# Revit family: PRD_FrankeWS_UrnlFlshngVlvs_BasicInstallationKitsForFlushingSystems_AQLN0006
name_source: partatom
category: Plumbing Fixtures
revit_build: Autodesk Revit 2018 (Build: 20190510_1515(x64)
units: mm (PartAtom-declared; Revit-internal decimal feet)

## family parameters
Cut with Voids When Loaded = No
Host = Face
OmniClass Number = 23.45.05.14.99
OmniClass Title = Other Sanitary Washing Plumbing Fixtures
Part Type = Normal
Room Calculation Point = No
Round Connector Dimension = Use Diameter
Shared = Yes

## types (1)
- AQLN0006
    Application = Urinal flushing
    AssetType = Fixed
    BIMObjectName = PRD_AR_UrinalFlushingValves_BasicInstallationKitsForFlushingSystems_AQLN0006
    Category = Pr_40_20_93_79, Urinal flushing valves
    Default Elevation = 1000 mm  [stored 3.28084 ft]
    Description = Basic installation kit for FLUSH-C manually operated and FLUSH-S non-touch, opto-electronically controlled urinal flush valve DN 15 for installation in walls. With wall mounting box and function block with integrated lockable water quantity regulator as well as remove plug for flushing and pressure testing.
    DurationUnit = year
    Features = Synthetic, in-wall installtation with box
    FlushValveMaterial = <By Category>
    FlushingRate = 0.0 L/s
    GrossWeight = 0.54 kg
    HasIntegralShutOffDevice = No
    HorizontalMounting = 110 mm  [stored 0.360892 ft]
    IfcExportAs = IfcValveType
    IfcExportType = FLUSHING
    InletSize = 15  [stored 0.0492126 ft]
    IsHighPressure = No
    Manufacturer = KWC Group AG
    ManufacturerName = KWC Group AG
    ManufacturerURL = www.kwc.com
    Material = Synthetic
    Model = AQLN0006
    ModelNumber = 2000107414
    ModelReference = AQLN0006
    NBSDescription = Urinal flushing valves
    NBSReference = 45-35-70/355
    Name = Urinal flush valve AQLN0006
    NetWeight = 0.51 kg
    NominalHeight = 0 mm  [stored 0 ft]
    NominalLength = 0 mm  [stored 0 ft]
    NominalWidth = 0 mm  [stored 0 ft]
    OutletSize = 15  [stored 0.0492126 ft]
    OverallDepth = 72 mm  [stored 0.23622 ft]
    ProductInformation = https://pim.kwc.com
    Type = built-in-box
    TypeOfMixing = no mixing
    URL = www.kwc.com
    Uniclass2015Code = Pr_40_20_93_79
    Uniclass2015Title = Urinal flushing valves
    Uniclass2015Version = Products v1.7
    Version = 1
    VerticalMounting = 102 mm  [stored 0.334646 ft]
    WarrantyDurationUnit = year

note: [stored X ft] marks values corroborated as IEEE doubles in the binary element streams (Revit-internal decimal feet)

## geometry (parser evidence)
native form markers: Sweep x1
no freeform markers — native parametric forms only
